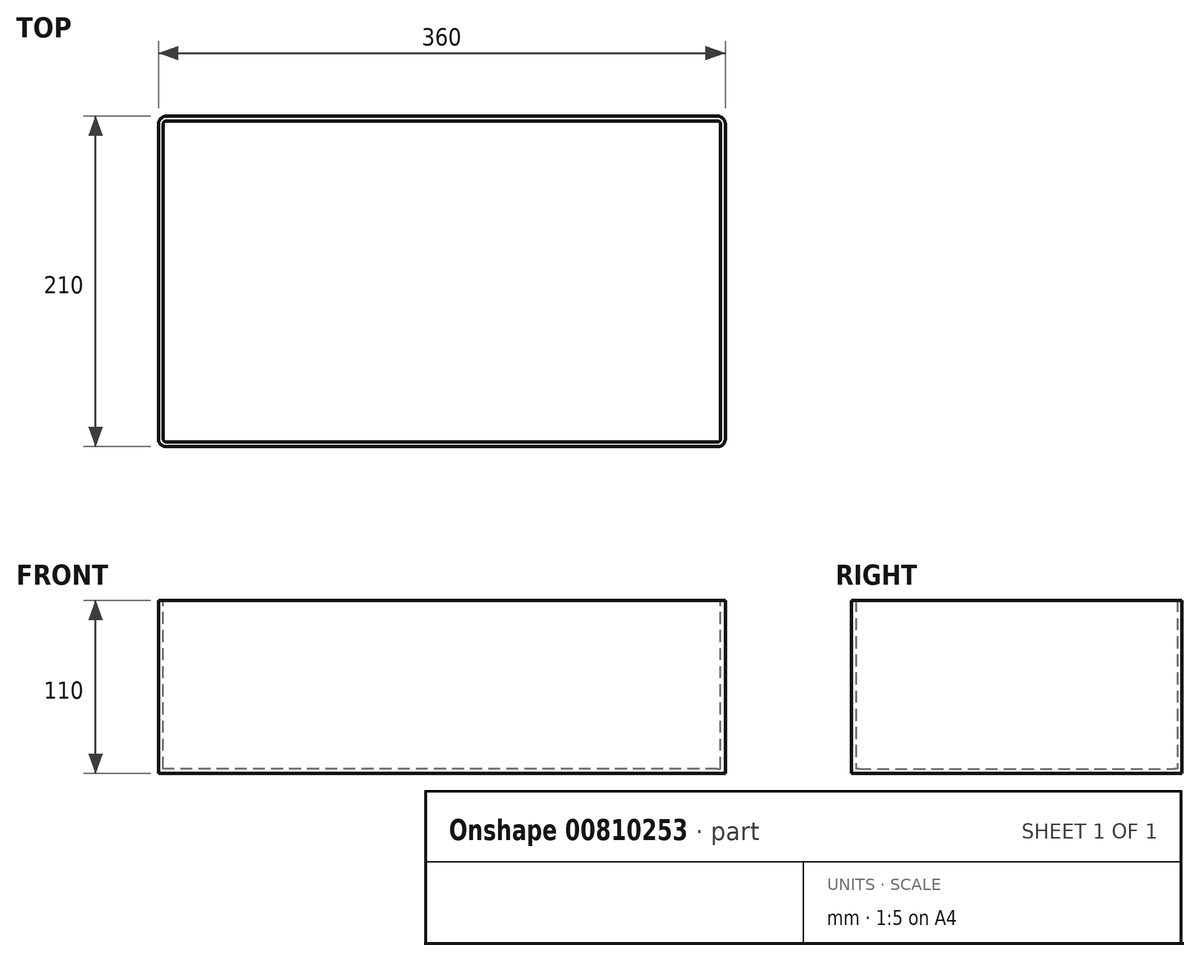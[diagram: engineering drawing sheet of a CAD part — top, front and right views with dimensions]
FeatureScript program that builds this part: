
annotation { "Feature Type Name" : "Feature", "Feature Type Description" : "" }
export const myFeature = defineFeature(function(context is Context, id is Id, definition is map)
    precondition{}
    {
        {
            var Q0;
            Q0=qCreatedBy(makeId("Top.planeOp"),FACE);
            var sketch = newSketch(context, id + "F0", { "sketchPlane" : qUnion([Q0])});
            skLineSegment(sketch, "E0.bottom", {"start": v(180, -105) * mm, "end": v(-180, -105) * mm});
            skLineSegment(sketch, "E0.top", {"start": v(180, 105) * mm, "end": v(-180, 105) * mm});
            skLineSegment(sketch, "E0.left", {"start": v(180, -105) * mm, "end": v(180, 105) * mm});
            skLineSegment(sketch, "E0.right", {"start": v(-180, -105) * mm, "end": v(-180, 105) * mm});
            skPoint(sketch, "E0.middle", {"position": v(0, 0) * mm});
            skSolve(sketch);
        }
        {
            var Q0;
            Q0=makeQuery(id+"F0.imprint","IMPRINT",FACE,{"disambiguationData":[TD([[makeQuery(id+"F0.imprint","IMPRINT",EDGE,{"derivedFrom":sQuery(id+"F0.wireOp",EDGE,"E0.bottom")}),-1.0]])]});
            extrude(context, id + "F1", {"entities" : qUnion([Q0]), "depth" : 110 * mm, "offsetDistance" : 25 * mm});
        }
        {
            var Q0;
            Q0=makeQuery(id+"F1.opExtrude","SWEPT_EDGE",EDGE,{"disambiguationData":[OSD([sQuery(id+"F0.wireOp",EDGE,"E0.top"),sQuery(id+"F0.wireOp",EDGE,"E0.right")])]});
            var Q1;
            Q1=makeQuery(id+"F1.opExtrude","SWEPT_EDGE",EDGE,{"disambiguationData":[OSD([sQuery(id+"F0.wireOp",EDGE,"E0.bottom"),sQuery(id+"F0.wireOp",EDGE,"E0.right")])]});
            var Q2;
            Q2=makeQuery(id+"F1.opExtrude","SWEPT_EDGE",EDGE,{"disambiguationData":[OSD([sQuery(id+"F0.wireOp",EDGE,"E0.bottom"),sQuery(id+"F0.wireOp",EDGE,"E0.left")])]});
            var Q3;
            Q3=makeQuery(id+"F1.opExtrude","SWEPT_EDGE",EDGE,{"disambiguationData":[OSD([sQuery(id+"F0.wireOp",EDGE,"E0.top"),sQuery(id+"F0.wireOp",EDGE,"E0.left")])]});
            fillet(context, id + "F2", {"entities" : qUnion([Q0, Q1, Q2, Q3]), "radius" : 5 * mm, "tangentPropagation" : true, "allowEdgeOverflow" : false});
        }
        {
            var Q0;
            Q0=makeQuery(id+"F1.opExtrude","CAP_FACE",FACE,{"disambiguationData":[OSD([sQuery(id+"F0.wireOp",EDGE,"E0.bottom"),sQuery(id+"F0.wireOp",EDGE,"E0.top"),sQuery(id+"F0.wireOp",EDGE,"E0.left"),sQuery(id+"F0.wireOp",EDGE,"E0.right")])],"isStart":false});
            shell(context, id + "F3", {"entities" : qUnion([Q0]), "thickness" : 3 * mm});
        }
    });
